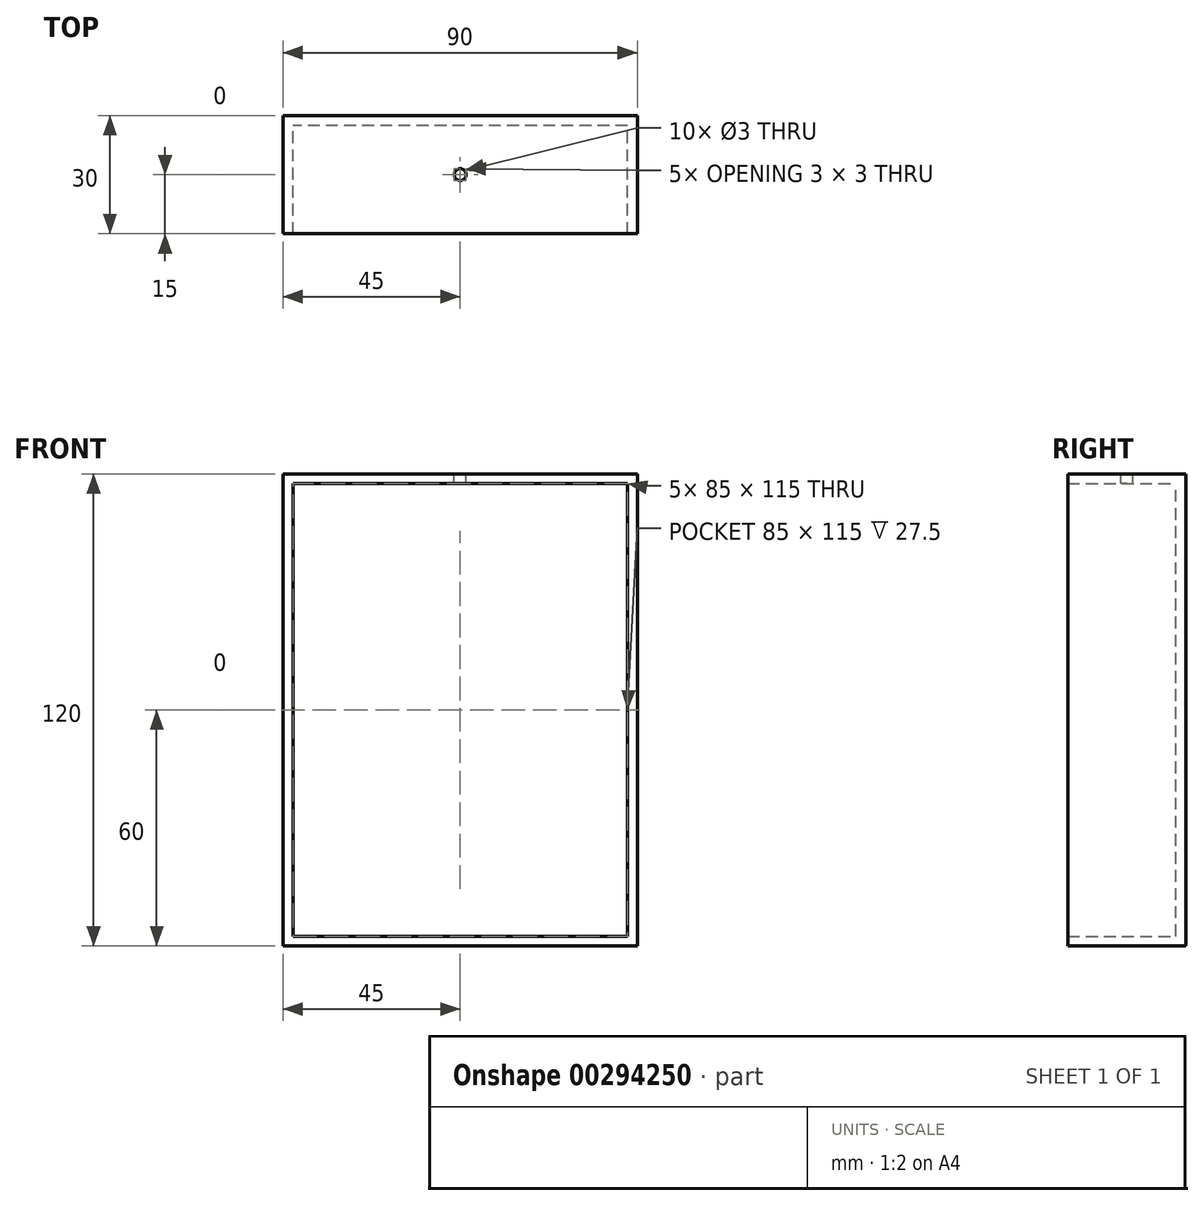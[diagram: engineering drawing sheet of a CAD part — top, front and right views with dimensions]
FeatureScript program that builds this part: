
annotation { "Feature Type Name" : "Feature", "Feature Type Description" : "" }
export const myFeature = defineFeature(function(context is Context, id is Id, definition is map)
    precondition{}
    {
        {
            var Q0;
            Q0=qCreatedBy(makeId("Front.planeOp"),FACE);
            var sketch = newSketch(context, id + "F0", { "sketchPlane" : qUnion([Q0])});
            skLineSegment(sketch, "E0.bottom", {"start": v(0, 0) * mm, "end": v(-90, 0) * mm});
            skLineSegment(sketch, "E0.top", {"start": v(0, 120) * mm, "end": v(-90, 120) * mm});
            skLineSegment(sketch, "E0.left", {"start": v(0, 0) * mm, "end": v(0, 120) * mm});
            skLineSegment(sketch, "E0.right", {"start": v(-90, 0) * mm, "end": v(-90, 120) * mm});
            skSolve(sketch);
        }
        {
            var Q0;
            Q0 = qSketchRegion(id + "F0", true);
            extrude(context, id + "F1", {"entities" : qUnion([Q0]), "depth" : 30 * mm});
        }
        {
            var Q0;
            Q0=makeQuery(id+"F1.opExtrude","CAP_FACE",FACE,{"disambiguationData":[OSD([sQuery(id+"F0.wireOp",EDGE,"E0.bottom"),sQuery(id+"F0.wireOp",EDGE,"E0.top"),sQuery(id+"F0.wireOp",EDGE,"E0.left"),sQuery(id+"F0.wireOp",EDGE,"E0.right")])],"isStart":false});
            shell(context, id + "F2", {"entities" : qUnion([Q0]), "thickness" : 2.5 * mm});
        }
        {
            var Q0;
            Q0=makeQuery(id+"F1.opExtrude","SWEPT_FACE",FACE,{"disambiguationData":[OSD([sQuery(id+"F0.wireOp",EDGE,"E0.top")])]});
            var sketch = newSketch(context, id + "F3", { "sketchPlane" : qUnion([Q0])});
            skLineSegment(sketch, "E1", {"start": v(-45, -30) * mm, "end": v(-45, 0) * mm, "construction": true});
            skLineSegment(sketch, "E2", {"start": v(-45, -15) * mm, "end": v(-90, -15) * mm, "construction": true});
            skCircle(sketch, "E3", {"center": v(-45, -15) * mm, "radius": 1.5 * mm});
            skSolve(sketch);
        }
        {
            var Q0;
            Q0 = qSketchRegion(id + "F3", true);
            extrude(context, id + "F4", {"entities" : qUnion([Q0]), "operationType" : NewBodyOperationType.REMOVE, "oppositeDirection" : true, "depth" : 25 * mm});
        }
    });
